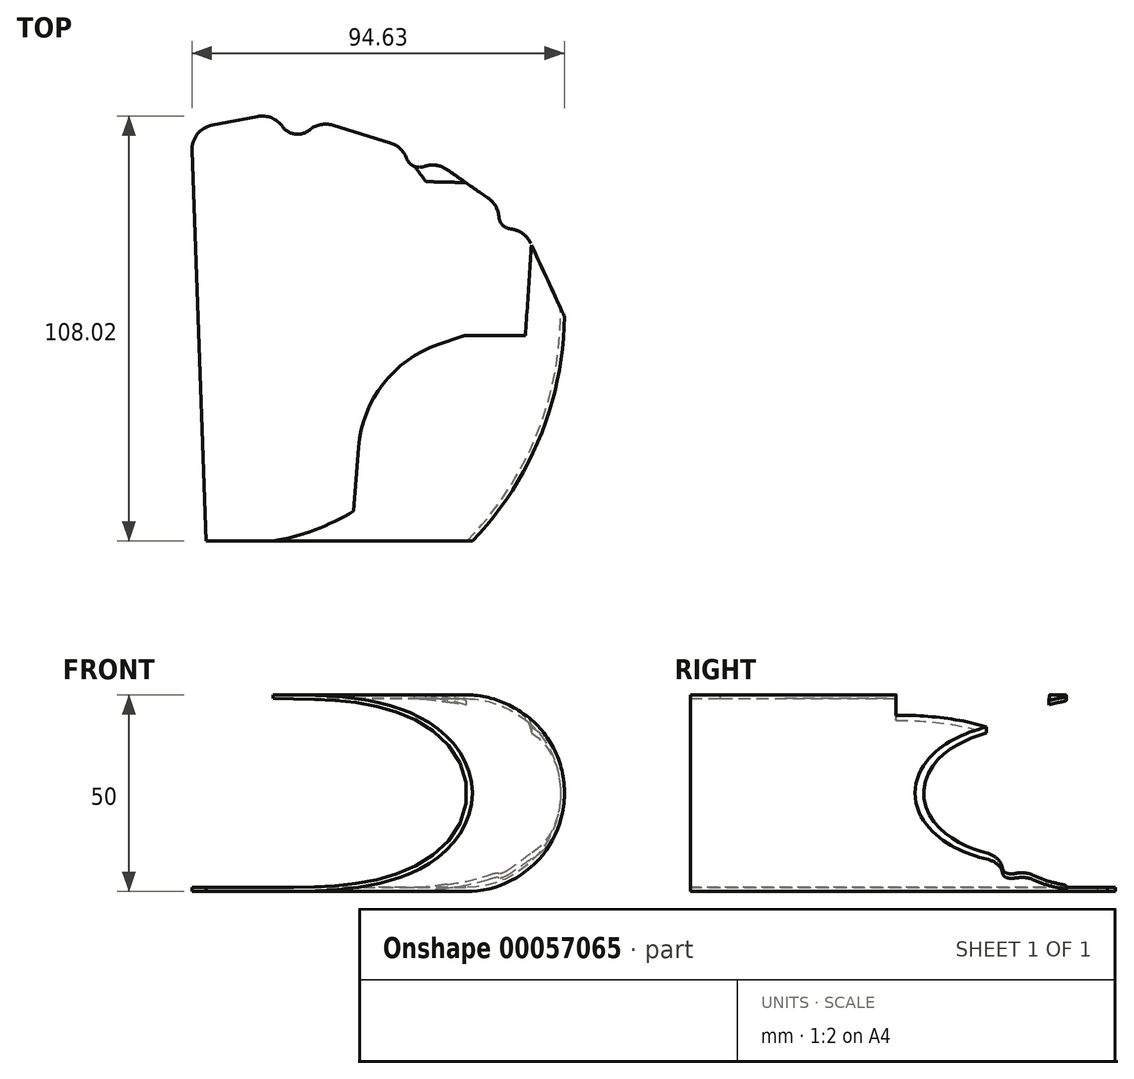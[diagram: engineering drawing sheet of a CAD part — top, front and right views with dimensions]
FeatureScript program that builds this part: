
annotation { "Feature Type Name" : "Feature", "Feature Type Description" : "" }
export const myFeature = defineFeature(function(context is Context, id is Id, definition is map)
    precondition{}
    {
        {
            var Q0;
            Q0=qCreatedBy(makeId("Top.planeOp"),FACE);
            var sketch = newSketch(context, id + "F0", { "sketchPlane" : qUnion([Q0])});
            skLineSegment(sketch, "E0", {"start": v(-126.98, -30.51) * mm, "end": v(-59.28, -30.51) * mm});
            skLineSegment(sketch, "E1", {"start": v(-44.48, 45.18) * mm, "end": v(-35.9, 26.58) * mm});
            skLineSegment(sketch, "E2", {"start": v(-55.25, 56.64) * mm, "end": v(-65.74, 63.93) * mm});
            skLineSegment(sketch, "E3", {"start": v(-80.11, 70.68) * mm, "end": v(-94.73, 75.17) * mm});
            skPoint(sketch, "E4.endSnap0", {"position": v(-113.06, 23) * mm});
            skLineSegment(sketch, "E5", {"start": v(-113.89, 77.39) * mm, "end": v(-125.4, 75.15) * mm});
            skArc(sketch, "E6", {"start": v(-59.28, -30.51) * mm, "mid": v(-42.16, -4.2) * mm, "end": v(-35.9, 26.58) * mm});
            skArc(sketch, "E7", {"start": v(-126.98, -30.51) * mm, "mid": v(-102.79, 10.22) * mm, "end": v(-129.83, 49.12) * mm});
            skPoint(sketch, "E7.first.point", {"position": v(-129.83, 49.12) * mm});
            skPoint(sketch, "E7.third.point", {"position": v(-103.34, 15.75) * mm});
            skArc(sketch, "E8", {"start": v(-107.5, 74.82) * mm, "mid": v(-104.28, 72.9) * mm, "end": v(-100.7, 73.95) * mm});
            skArc(sketch, "E9", {"start": v(-76, 66.78) * mm, "mid": v(-74.2, 64.8) * mm, "end": v(-71.53, 64.68) * mm});
            skArc(sketch, "E10", {"start": v(-52.54, 51.88) * mm, "mid": v(-51.61, 49.82) * mm, "end": v(-49.59, 48.84) * mm});
            skLineSegment(sketch, "E11", {"start": v(-130.53, 68.7) * mm, "end": v(-129.83, 49.12) * mm});
            skPoint(sketch, "E12.visualSharp", {"position": v(-130.72, 74.12) * mm});
            skArc(sketch, "E12.filletArc", {"start": v(-125.4, 75.15) * mm, "mid": v(-129.15, 72.87) * mm, "end": v(-130.53, 68.7) * mm});
            skPoint(sketch, "E13.visualSharp", {"position": v(-108.24, 78.49) * mm});
            skArc(sketch, "E13.filletArc", {"start": v(-107.5, 74.82) * mm, "mid": v(-110.3, 77.05) * mm, "end": v(-113.89, 77.39) * mm});
            skPoint(sketch, "E14.visualSharp", {"position": v(-99.15, 76.53) * mm});
            skArc(sketch, "E14.filletArc", {"start": v(-94.73, 75.17) * mm, "mid": v(-97.87, 75.32) * mm, "end": v(-100.7, 73.95) * mm});
            skPoint(sketch, "E15.visualSharp", {"position": v(-75.92, 69.4) * mm});
            skArc(sketch, "E15.filletArc", {"start": v(-76, 66.78) * mm, "mid": v(-77.6, 69.21) * mm, "end": v(-80.11, 70.68) * mm});
            skPoint(sketch, "E16.visualSharp", {"position": v(-69.52, 66.55) * mm});
            skArc(sketch, "E16.filletArc", {"start": v(-65.74, 63.93) * mm, "mid": v(-68.54, 65) * mm, "end": v(-71.53, 64.68) * mm});
            skPoint(sketch, "E17.visualSharp", {"position": v(-51.78, 54.23) * mm});
            skArc(sketch, "E17.filletArc", {"start": v(-52.54, 51.88) * mm, "mid": v(-53.35, 54.57) * mm, "end": v(-55.25, 56.64) * mm});
            skPoint(sketch, "E18.visualSharp", {"position": v(-46.7, 50) * mm});
            skArc(sketch, "E18.filletArc", {"start": v(-44.48, 45.18) * mm, "mid": v(-46.55, 47.69) * mm, "end": v(-49.59, 48.84) * mm});
            skPoint(sketch, "E19.visualSharp", {"position": v(-35.9, 26.58) * mm});
            skLineSegment(sketch, "E20", {"start": v(-129.83, 49.12) * mm, "end": v(-126.98, -30.51) * mm});
            skSolve(sketch);
        }
        {
            var Q0;
            Q0=makeQuery(id+"F0.imprint","IMPRINT",FACE,{"disambiguationData":[TD([[makeQuery(id+"F0.imprint","IMPRINT",EDGE,{"derivedFrom":sQuery(id+"F0.wireOp",EDGE,"E0")}),1.0]])]});
            var Q1;
            Q1=makeQuery(id+"F0.imprint","IMPRINT",FACE,{"disambiguationData":[TD([[makeQuery(id+"F0.imprint","IMPRINT",EDGE,{"derivedFrom":sQuery(id+"F0.wireOp",EDGE,"E7")}),1.0]])]});
            extrude(context, id + "F1", {"entities" : qUnion([Q0, Q1]), "depth" : 50 * mm});
        }
        {
            var Q0;
            Q0=makeQuery(id+"F1.opExtrude","CAP_EDGE",EDGE,{"disambiguationData":[OSD([sQuery(id+"F0.wireOp",EDGE,"E6")])],"isStart":false});
            var Q1;
            Q1=makeQuery(id+"F1.opExtrude","CAP_EDGE",EDGE,{"disambiguationData":[OSD([sQuery(id+"F0.wireOp",EDGE,"E6")])],"isStart":true});
            fillet(context, id + "F2", {"entities" : qUnion([Q0, Q1]), "radius" : 25 * mm, "tangentPropagation" : true, "allowEdgeOverflow" : false});
        }
        {
            var Q0;
            Q0=makeQuery(id+"F1.opExtrude","SWEPT_FACE",FACE,{"disambiguationData":[OSD([sQuery(id+"F0.wireOp",EDGE,"E0")])]});
            var Q1;
            Q1=makeQuery(id+"F1.opExtrude","SWEPT_FACE",FACE,{"disambiguationData":[OSD([sQuery(id+"F0.wireOp",EDGE,"E11"),sQuery(id+"F0.wireOp",EDGE,"E20")])]});
            var Q2;
            Q2=makeQuery(id+"F1.opExtrude","SWEPT_FACE",FACE,{"disambiguationData":[OSD([sQuery(id+"F0.wireOp",EDGE,"E12.filletArc")])]});
            var Q3;
            Q3=makeQuery(id+"F1.opExtrude","SWEPT_FACE",FACE,{"disambiguationData":[OSD([sQuery(id+"F0.wireOp",EDGE,"E5")])]});
            var Q4;
            Q4=makeQuery(id+"F1.opExtrude","SWEPT_FACE",FACE,{"disambiguationData":[OSD([sQuery(id+"F0.wireOp",EDGE,"E8")])]});
            var Q5;
            Q5=makeQuery(id+"F1.opExtrude","SWEPT_FACE",FACE,{"disambiguationData":[OSD([sQuery(id+"F0.wireOp",EDGE,"E13.filletArc")])]});
            var Q6;
            Q6=makeQuery(id+"F1.opExtrude","SWEPT_FACE",FACE,{"disambiguationData":[OSD([sQuery(id+"F0.wireOp",EDGE,"E14.filletArc")])]});
            var Q7;
            Q7=makeQuery(id+"F1.opExtrude","SWEPT_FACE",FACE,{"disambiguationData":[OSD([sQuery(id+"F0.wireOp",EDGE,"E1")])]});
            var Q8;
            Q8=makeQuery(id+"F1.opExtrude","SWEPT_FACE",FACE,{"disambiguationData":[OSD([sQuery(id+"F0.wireOp",EDGE,"E18.filletArc")])]});
            var Q9;
            Q9=makeQuery(id+"F1.opExtrude","SWEPT_FACE",FACE,{"disambiguationData":[OSD([sQuery(id+"F0.wireOp",EDGE,"E10")])]});
            var Q10;
            Q10=makeQuery(id+"F1.opExtrude","SWEPT_FACE",FACE,{"disambiguationData":[OSD([sQuery(id+"F0.wireOp",EDGE,"E17.filletArc")])]});
            var Q11;
            Q11=makeQuery(id+"F1.opExtrude","SWEPT_FACE",FACE,{"disambiguationData":[OSD([sQuery(id+"F0.wireOp",EDGE,"E2")])]});
            var Q12;
            Q12=makeQuery(id+"F1.opExtrude","SWEPT_FACE",FACE,{"disambiguationData":[OSD([sQuery(id+"F0.wireOp",EDGE,"E16.filletArc")])]});
            var Q13;
            Q13=makeQuery(id+"F1.opExtrude","SWEPT_FACE",FACE,{"disambiguationData":[OSD([sQuery(id+"F0.wireOp",EDGE,"E9")])]});
            var Q14;
            Q14=makeQuery(id+"F1.opExtrude","SWEPT_FACE",FACE,{"disambiguationData":[OSD([sQuery(id+"F0.wireOp",EDGE,"E3")])]});
            var Q15;
            Q15=makeQuery(id+"F1.opExtrude","SWEPT_FACE",FACE,{"disambiguationData":[OSD([sQuery(id+"F0.wireOp",EDGE,"E15.filletArc")])]});
            shell(context, id + "F3", {"entities" : qUnion([Q0, Q1, Q2, Q3, Q4, Q5, Q6, Q7, Q8, Q9, Q10, Q11, Q12, Q13, Q14, Q15]), "thickness" : 1 * mm});
        }
        {
            var Q0;
            Q0=makeQuery(id+"F1.opExtrude","CAP_FACE",FACE,{"disambiguationData":[OSD([sQuery(id+"F0.wireOp",EDGE,"E0"),sQuery(id+"F0.wireOp",EDGE,"E1"),sQuery(id+"F0.wireOp",EDGE,"E2"),sQuery(id+"F0.wireOp",EDGE,"E3"),sQuery(id+"F0.wireOp",EDGE,"E5"),sQuery(id+"F0.wireOp",EDGE,"E6"),sQuery(id+"F0.wireOp",EDGE,"E8"),sQuery(id+"F0.wireOp",EDGE,"E9"),sQuery(id+"F0.wireOp",EDGE,"E10"),sQuery(id+"F0.wireOp",EDGE,"E11"),sQuery(id+"F0.wireOp",EDGE,"E12.filletArc"),sQuery(id+"F0.wireOp",EDGE,"E13.filletArc"),sQuery(id+"F0.wireOp",EDGE,"E14.filletArc"),sQuery(id+"F0.wireOp",EDGE,"E15.filletArc"),sQuery(id+"F0.wireOp",EDGE,"E16.filletArc"),sQuery(id+"F0.wireOp",EDGE,"E17.filletArc"),sQuery(id+"F0.wireOp",EDGE,"E18.filletArc"),sQuery(id+"F0.wireOp",EDGE,"E20")])],"isStart":false});
            var sketch = newSketch(context, id + "F4", { "sketchPlane" : qUnion([Q0])});
            skLineSegment(sketch, "E21", {"start": v(-89.78, -27.89) * mm, "end": v(-88.16, -6.65) * mm});
            skLineSegment(sketch, "E22", {"start": v(-67.94, 19.46) * mm, "end": v(-49.3, 25.83) * mm});
            skLineSegment(sketch, "E23", {"start": v(-48.49, 25.96) * mm, "end": v(-25.05, 25.96) * mm});
            skLineSegment(sketch, "E24", {"start": v(-25.05, 25.96) * mm, "end": v(-29.43, -31.9) * mm});
            skLineSegment(sketch, "E25", {"start": v(-29.43, -31.9) * mm, "end": v(-87.34, -30.57) * mm});
            skLineSegment(sketch, "E26", {"start": v(-25.05, 25.96) * mm, "end": v(-21.83, 94.65) * mm});
            skLineSegment(sketch, "E27", {"start": v(-21.83, 94.65) * mm, "end": v(-157.82, 98.55) * mm});
            skLineSegment(sketch, "E28", {"start": v(-157.82, 98.55) * mm, "end": v(-141.25, -38.94) * mm});
            skLineSegment(sketch, "E29", {"start": v(-141.25, -38.94) * mm, "end": v(-88.49, -30.27) * mm});
            skPoint(sketch, "E30.visualSharp", {"position": v(-86.66, 13.07) * mm});
            skArc(sketch, "E30.filletArc", {"start": v(-67.94, 19.46) * mm, "mid": v(-81.97, 9.44) * mm, "end": v(-88.16, -6.65) * mm});
            skPoint(sketch, "E31.visualSharp", {"position": v(-89.98, -30.51) * mm});
            skArc(sketch, "E31.filletArc", {"start": v(-89.78, -27.89) * mm, "mid": v(-89.14, -29.75) * mm, "end": v(-87.34, -30.57) * mm});
            skPoint(sketch, "E32.visualSharp", {"position": v(-48.9, 25.96) * mm});
            skArc(sketch, "E32.filletArc", {"start": v(-48.49, 25.96) * mm, "mid": v(-48.9, 25.93) * mm, "end": v(-49.3, 25.83) * mm});
            skSolve(sketch);
        }
        {
            var Q0;
            {var subQ2=sQuery(id+"F4.wireOp",EDGE,"E21");Q0=makeQuery(id+"F4.imprint","IMPRINT",FACE,{"disambiguationData":[TD([[makeQuery(id+"F4.imprint","IMPRINT",EDGE,{"derivedFrom":subQ2}),1.0]])]});}
            extrude(context, id + "F5", {"entities" : qUnion([Q0]), "operationType" : NewBodyOperationType.REMOVE, "oppositeDirection" : true, "depth" : 25 * mm});
        }
        {
            var Q0;
            Q0=makeQuery(id+"F1.opExtrude","CAP_FACE",FACE,{"disambiguationData":[OSD([sQuery(id+"F0.wireOp",EDGE,"E0"),sQuery(id+"F0.wireOp",EDGE,"E1"),sQuery(id+"F0.wireOp",EDGE,"E2"),sQuery(id+"F0.wireOp",EDGE,"E3"),sQuery(id+"F0.wireOp",EDGE,"E5"),sQuery(id+"F0.wireOp",EDGE,"E6"),sQuery(id+"F0.wireOp",EDGE,"E8"),sQuery(id+"F0.wireOp",EDGE,"E9"),sQuery(id+"F0.wireOp",EDGE,"E10"),sQuery(id+"F0.wireOp",EDGE,"E11"),sQuery(id+"F0.wireOp",EDGE,"E12.filletArc"),sQuery(id+"F0.wireOp",EDGE,"E13.filletArc"),sQuery(id+"F0.wireOp",EDGE,"E14.filletArc"),sQuery(id+"F0.wireOp",EDGE,"E15.filletArc"),sQuery(id+"F0.wireOp",EDGE,"E16.filletArc"),sQuery(id+"F0.wireOp",EDGE,"E17.filletArc"),sQuery(id+"F0.wireOp",EDGE,"E18.filletArc"),sQuery(id+"F0.wireOp",EDGE,"E20")])],"isStart":false});
            var sketch = newSketch(context, id + "F6", { "sketchPlane" : qUnion([Q0])});
            skLineSegment(sketch, "E33", {"start": v(-61.18, 21.77) * mm, "end": v(-45.8, 21.77) * mm});
            skLineSegment(sketch, "E34", {"start": v(-45.8, 21.77) * mm, "end": v(-43.27, 60.2) * mm});
            skLineSegment(sketch, "E35", {"start": v(-43.27, 60.2) * mm, "end": v(-78.31, 61) * mm});
            skLineSegment(sketch, "E36", {"start": v(-78.31, 61) * mm, "end": v(-61.18, 21.77) * mm});
            skSolve(sketch);
        }
        {
            var Q0;
            Q0=makeQuery(id+"F6.imprint","IMPRINT",FACE,{"disambiguationData":[TD([[makeQuery(id+"F6.imprint","IMPRINT",EDGE,{"derivedFrom":sQuery(id+"F6.wireOp",EDGE,"E33")}),1.0]])]});
            extrude(context, id + "F7", {"entities" : qUnion([Q0]), "operationType" : NewBodyOperationType.REMOVE, "oppositeDirection" : true, "depth" : 15 * mm});
        }
        {
            var Q0;
            Q0=makeQuery(id+"F7.boolean.opBoolean","COPY",EDGE,{"derivedFrom":makeQuery(id+"F7.opExtrude","CAP_EDGE",EDGE,{"disambiguationData":[OSD([sQuery(id+"F6.wireOp",EDGE,"E33")])],"isStart":false})});
            var Q1;
            {var subQ0=sQuery(id+"F4.wireOp",EDGE,"E22");var subQ1=sQuery(id+"F0.wireOp",EDGE,"E20");var subQ2=sQuery(id+"F0.wireOp",EDGE,"E18.filletArc");var subQ3=sQuery(id+"F0.wireOp",EDGE,"E17.filletArc");var subQ4=sQuery(id+"F0.wireOp",EDGE,"E16.filletArc");var subQ5=sQuery(id+"F0.wireOp",EDGE,"E15.filletArc");var subQ6=sQuery(id+"F0.wireOp",EDGE,"E14.filletArc");var subQ7=sQuery(id+"F0.wireOp",EDGE,"E13.filletArc");var subQ8=sQuery(id+"F0.wireOp",EDGE,"E12.filletArc");var subQ9=sQuery(id+"F0.wireOp",EDGE,"E11");var subQ10=sQuery(id+"F0.wireOp",EDGE,"E10");var subQ11=sQuery(id+"F0.wireOp",EDGE,"E9");var subQ12=sQuery(id+"F0.wireOp",EDGE,"E8");var subQ13=sQuery(id+"F0.wireOp",EDGE,"E6");var subQ14=sQuery(id+"F0.wireOp",EDGE,"E5");var subQ15=sQuery(id+"F0.wireOp",EDGE,"E3");var subQ16=sQuery(id+"F0.wireOp",EDGE,"E2");var subQ17=sQuery(id+"F0.wireOp",EDGE,"E1");var subQ18=sQuery(id+"F0.wireOp",EDGE,"E0");Q1=makeQuery(id+"F7.boolean.opBoolean","MERGE",EDGE,{"derivedFrom":[makeQuery(id+"F5.boolean.opBoolean","COPY",EDGE,{"derivedFrom":makeQuery(id+"F5.opExtrude","SWEPT_EDGE",EDGE,{"disambiguationData":[OSD([subQ18,subQ17,subQ16,subQ15,subQ14,subQ13,subQ12,subQ11,subQ10,subQ9,subQ8,subQ7,subQ6,subQ5,subQ4,subQ3,subQ2,subQ1,subQ0])]})}),makeQuery(id+"F7.opExtrude","SWEPT_EDGE",EDGE,{"disambiguationData":[OSD([subQ18,subQ17,subQ16,subQ15,subQ14,subQ13,subQ12,subQ11,subQ10,subQ9,subQ8,subQ7,subQ6,subQ5,subQ4,subQ3,subQ2,subQ1,subQ0,sQuery(id+"F6.wireOp",EDGE,"E33"),sQuery(id+"F6.wireOp",EDGE,"E36")])]})]});}
            fillet(context, id + "F8", {"entities" : qUnion([Q0, Q1]), "radius" : 3 * mm, "tangentPropagation" : true, "allowEdgeOverflow" : false});
        }
    });
